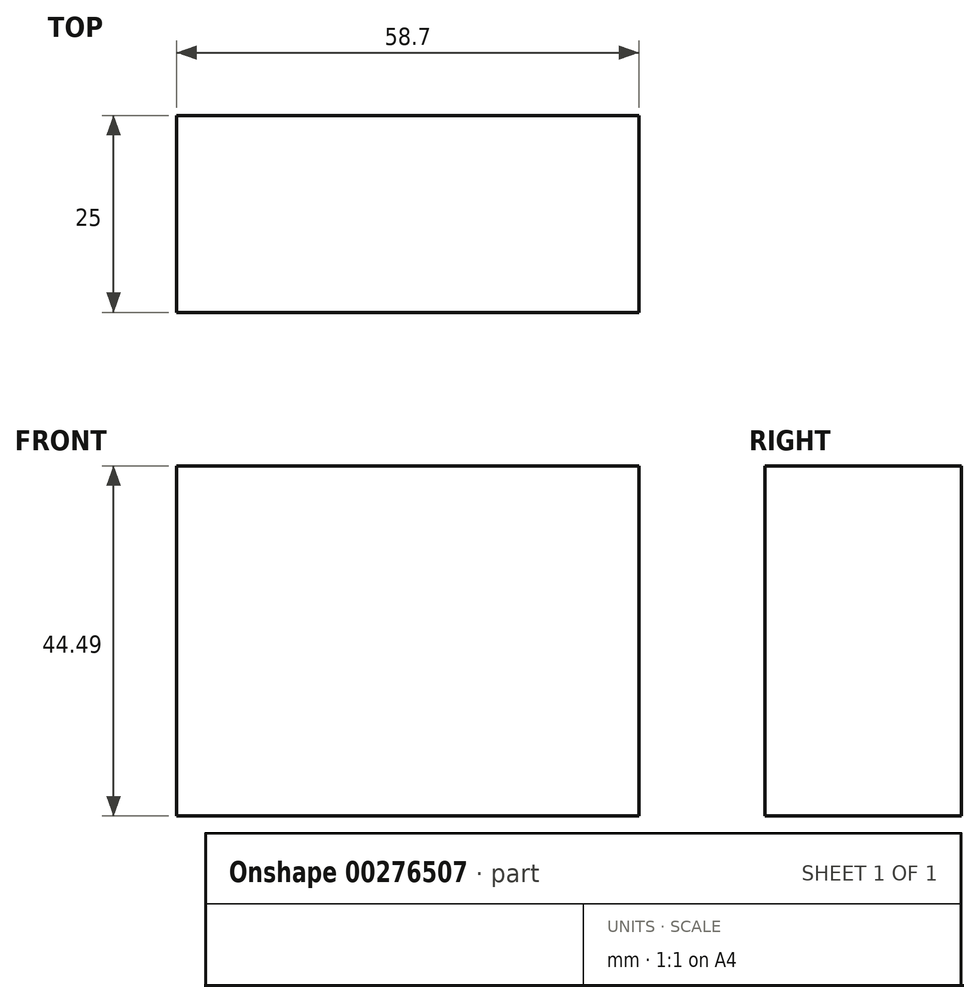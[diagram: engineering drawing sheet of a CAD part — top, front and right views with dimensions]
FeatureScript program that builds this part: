
annotation { "Feature Type Name" : "Feature", "Feature Type Description" : "" }
export const myFeature = defineFeature(function(context is Context, id is Id, definition is map)
    precondition{}
    {
        {
            var Q0;
            Q0=qCreatedBy(makeId("Front.planeOp"),FACE);
            var sketch = newSketch(context, id + "F0", { "sketchPlane" : qUnion([Q0])});
            skLineSegment(sketch, "E0.bottom", {"start": v(-30.73, 23.85) * mm, "end": v(27.97, 23.85) * mm});
            skLineSegment(sketch, "E0.top", {"start": v(-30.73, -20.64) * mm, "end": v(27.97, -20.64) * mm});
            skLineSegment(sketch, "E0.left", {"start": v(-30.73, 23.85) * mm, "end": v(-30.73, -20.64) * mm});
            skLineSegment(sketch, "E0.right", {"start": v(27.97, 23.85) * mm, "end": v(27.97, -20.64) * mm});
            skSolve(sketch);
        }
        {
            var Q0;
            Q0=makeQuery(id+"F0.imprint","IMPRINT",FACE,{"disambiguationData":[TD([[makeQuery(id+"F0.imprint","IMPRINT",EDGE,{"derivedFrom":sQuery(id+"F0.wireOp",EDGE,"E0.bottom")}),-1.0]])]});
            extrude(context, id + "F1", {"entities" : qUnion([Q0]), "depth" : 25 * mm});
        }
    });
